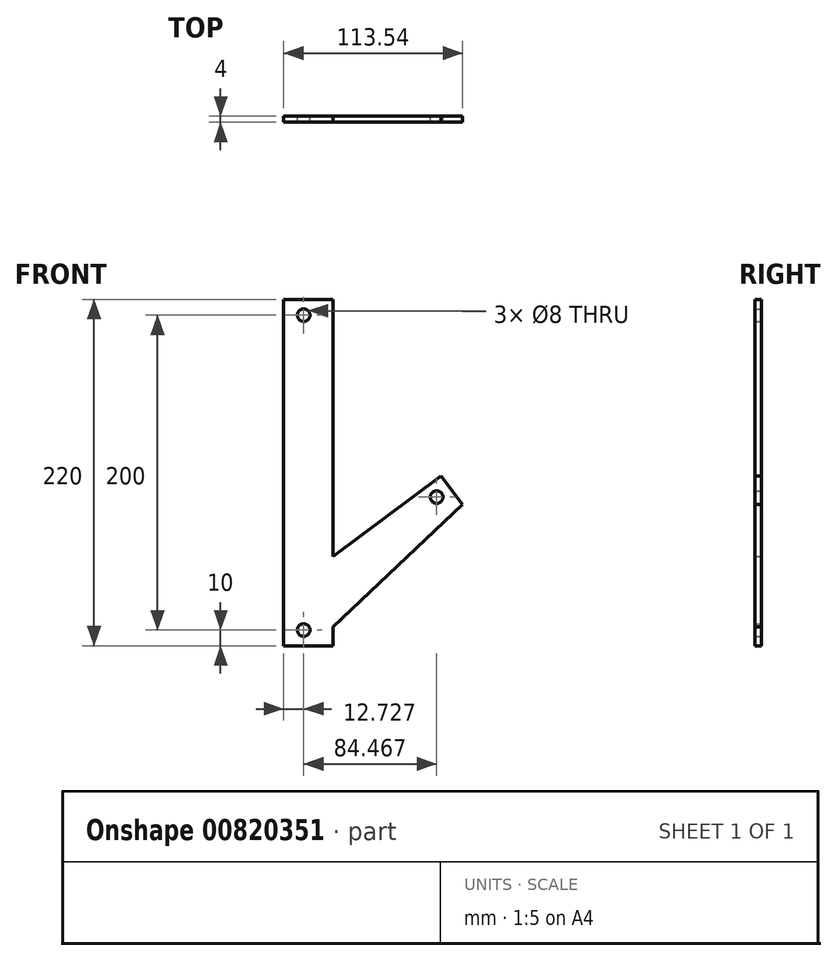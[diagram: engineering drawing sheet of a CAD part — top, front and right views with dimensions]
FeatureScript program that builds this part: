
annotation { "Feature Type Name" : "Feature", "Feature Type Description" : "" }
export const myFeature = defineFeature(function(context is Context, id is Id, definition is map)
    precondition{}
    {
        {
            var Q0;
            Q0=qCreatedBy(makeId("Front.planeOp"),FACE);
            var sketch = newSketch(context, id + "F0", { "sketchPlane" : qUnion([Q0])});
            skLineSegment(sketch, "E0.bottom", {"start": v(0, 0) * mm, "end": v(31.36, 0) * mm});
            skLineSegment(sketch, "E0.top", {"start": v(0, 220) * mm, "end": v(31.36, 220) * mm});
            skLineSegment(sketch, "E0.left", {"start": v(0, 0) * mm, "end": v(0, 220) * mm});
            skLineSegment(sketch, "E0.right", {"start": v(31.36, 0) * mm, "end": v(31.36, 12.08) * mm});
            skCircle(sketch, "E1", {"center": v(12.73, 10) * mm, "radius": 4 * mm});
            skCircle(sketch, "E2", {"center": v(12.73, 210) * mm, "radius": 4 * mm});
            skLineSegment(sketch, "E3", {"start": v(31.36, 56.86) * mm, "end": v(100, 107.9) * mm});
            skLineSegment(sketch, "E4", {"start": v(100, 107.9) * mm, "end": v(113.54, 89.7) * mm});
            skLineSegment(sketch, "E5", {"start": v(113.54, 89.7) * mm, "end": v(31.36, 12.08) * mm});
            skLineSegment(sketch, "E6.trimOffspring", {"start": v(31.36, 56.86) * mm, "end": v(31.36, 220) * mm});
            skCircle(sketch, "E7", {"center": v(97.2, 94.47) * mm, "radius": 4 * mm});
            skLineSegment(sketch, "E8", {"start": v(97.2, 94.47) * mm, "end": v(12.73, 10) * mm, "construction": true});
            skLineSegment(sketch, "E9", {"start": v(12.73, 10) * mm, "end": v(12.73, 210) * mm, "construction": true});
            skSolve(sketch);
        }
        {
            var Q0;
            Q0=makeQuery(id+"F0.imprint","IMPRINT",FACE,{"disambiguationData":[TD([[makeQuery(id+"F0.imprint","IMPRINT",EDGE,{"derivedFrom":sQuery(id+"F0.wireOp",EDGE,"E0.bottom")}),1.0]])]});
            extrude(context, id + "F1", {"entities" : qUnion([Q0]), "depth" : 4 * mm, "offsetDistance" : 25 * mm});
        }
    });
